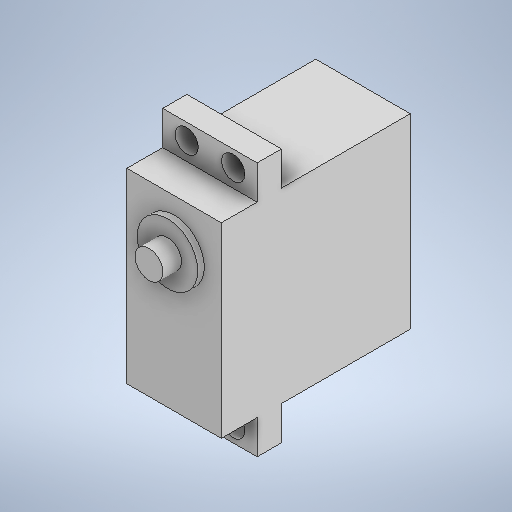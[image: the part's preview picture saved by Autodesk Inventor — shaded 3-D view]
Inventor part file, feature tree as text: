
AUTODESK INVENTOR PART (.ipt)
format: ipt  version: 2025.1 (Build 291241000, 241)  size: 288,768 bytes
history: native  units: mm
features: extrude x6, sketch x6
ambient origin geometry x8: Origin, YZ Plane, XZ Plane, XY Plane, X Axis, Y Axis, Z Axis, Center Point
bodies: Volumenkörper1 (feature_tree)
feature tree (12):
  extrude  "Extrusion1"  Depth=20.3mm
  extrude  "Extrusion2"  Depth=40.6mm
  extrude  "Extrusion3"  TaperAngle=0.0deg  [1 undecoded]
  extrude  "Extrusion4"  Depth=1.4mm
  extrude  "Extrusion5"  TaperAngle=0.0deg  [1 undecoded]
  extrude  "Extrusion6"  Depth=5.2mm
  sketch  "Skizze1"  dims[d0=40.1mm d1=20.3mm]
  sketch  "Skizze2"  dims[d2=40.6mm d3=0.0mm d4=13.0mm]
  sketch  "Skizze3"  dims[d5=30.0mm d6=0.0mm]
  sketch  "Skizze4"  dims[d7=1.4mm d8=0.0mm d9=6.0mm]
  sketch  "Skizze5"  dims[d10=4.0mm d11=0.0mm d12=0.0mm]
  sketch  "Skizze6"  dims[d13=7.7mm d14=5.2mm d15=7.3mm d16=0.0mm d17=0.0mm d18=7.3mm d19=0.0mm d20=7.7mm d21=5.2mm d22=5.0mm d23=10.0mm d27=7.3mm d28=0.0mm d29=47.8mm d30=3.45mm]
note: 2 required parameter values undecoded (feature->parameter linkage not recoverable at this tier; creation-order binding heuristic only, values carry confidence <= 0.55)
